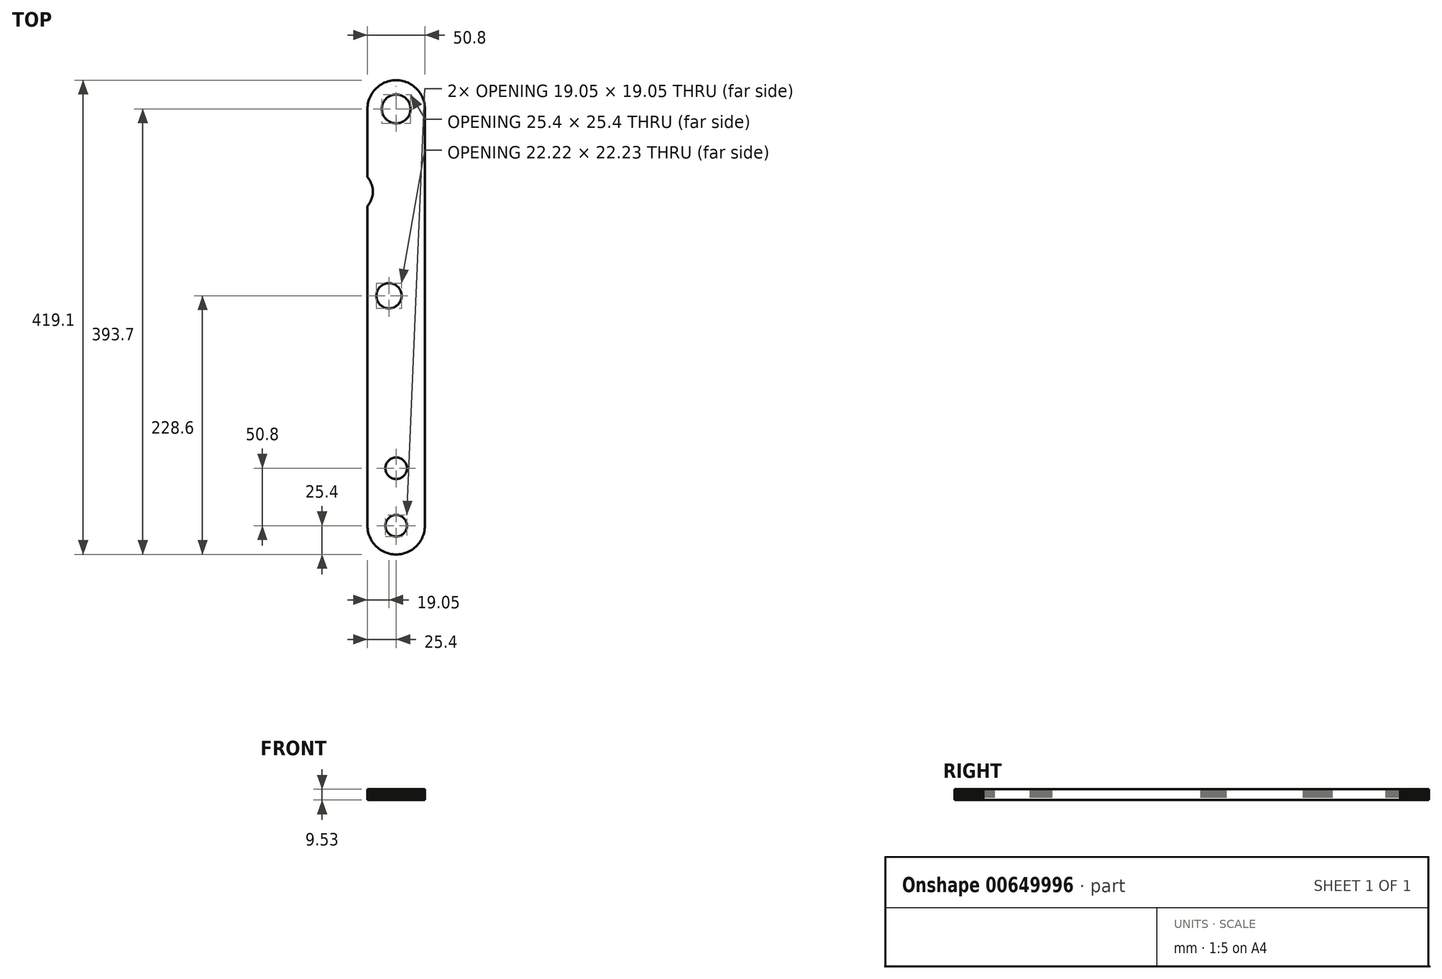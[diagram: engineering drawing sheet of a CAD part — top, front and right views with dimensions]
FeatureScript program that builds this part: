
annotation { "Feature Type Name" : "Feature", "Feature Type Description" : "" }
export const myFeature = defineFeature(function(context is Context, id is Id, definition is map)
    precondition{}
    {
        {
            var Q0;
            Q0=qCreatedBy(makeId("Top.planeOp"),FACE);
            var sketch = newSketch(context, id + "F0", { "sketchPlane" : qUnion([Q0])});
            skLineSegment(sketch, "E0", {"start": v(25.4, 184.15) * mm, "end": v(25.36, 185.63) * mm});
            skLineSegment(sketch, "E1", {"start": v(25.36, 185.63) * mm, "end": v(25.23, 187.1) * mm});
            skLineSegment(sketch, "E2", {"start": v(25.23, 187.1) * mm, "end": v(25.02, 188.55) * mm});
            skLineSegment(sketch, "E3", {"start": v(25.02, 188.55) * mm, "end": v(24.72, 190.01) * mm});
            skLineSegment(sketch, "E4", {"start": v(24.72, 190.01) * mm, "end": v(24.34, 191.43) * mm});
            skLineSegment(sketch, "E5", {"start": v(24.34, 191.43) * mm, "end": v(23.88, 192.83) * mm});
            skLineSegment(sketch, "E6", {"start": v(23.88, 192.83) * mm, "end": v(23.33, 194.2) * mm});
            skLineSegment(sketch, "E7", {"start": v(23.33, 194.2) * mm, "end": v(22.71, 195.56) * mm});
            skLineSegment(sketch, "E8", {"start": v(22.71, 195.56) * mm, "end": v(22.01, 196.85) * mm});
            skLineSegment(sketch, "E9", {"start": v(22.01, 196.85) * mm, "end": v(21.23, 198.1) * mm});
            skLineSegment(sketch, "E10", {"start": v(21.23, 198.1) * mm, "end": v(20.38, 199.33) * mm});
            skLineSegment(sketch, "E11", {"start": v(20.38, 199.33) * mm, "end": v(19.47, 200.47) * mm});
            skLineSegment(sketch, "E12", {"start": v(19.47, 200.47) * mm, "end": v(18.48, 201.57) * mm});
            skLineSegment(sketch, "E13", {"start": v(18.48, 201.57) * mm, "end": v(17.44, 202.63) * mm});
            skLineSegment(sketch, "E14", {"start": v(17.44, 202.63) * mm, "end": v(16.34, 203.6) * mm});
            skLineSegment(sketch, "E15", {"start": v(16.34, 203.6) * mm, "end": v(15.18, 204.53) * mm});
            skLineSegment(sketch, "E16", {"start": v(15.18, 204.53) * mm, "end": v(13.97, 205.38) * mm});
            skLineSegment(sketch, "E17", {"start": v(13.97, 205.38) * mm, "end": v(12.7, 206.14) * mm});
            skLineSegment(sketch, "E18", {"start": v(12.7, 206.14) * mm, "end": v(11.4, 206.84) * mm});
            skLineSegment(sketch, "E19", {"start": v(11.4, 206.84) * mm, "end": v(10.08, 207.48) * mm});
            skLineSegment(sketch, "E20", {"start": v(10.08, 207.48) * mm, "end": v(8.7, 208.03) * mm});
            skLineSegment(sketch, "E21", {"start": v(8.7, 208.03) * mm, "end": v(7.3, 208.5) * mm});
            skLineSegment(sketch, "E22", {"start": v(7.3, 208.5) * mm, "end": v(5.86, 208.87) * mm});
            skLineSegment(sketch, "E23", {"start": v(5.86, 208.87) * mm, "end": v(4.42, 209.17) * mm});
            skLineSegment(sketch, "E24", {"start": v(4.42, 209.17) * mm, "end": v(2.96, 209.38) * mm});
            skLineSegment(sketch, "E25", {"start": v(2.96, 209.38) * mm, "end": v(1.48, 209.5) * mm});
            skLineSegment(sketch, "E26", {"start": v(1.48, 209.5) * mm, "end": v(0, 209.55) * mm});
            skLineSegment(sketch, "E27", {"start": v(0, 209.55) * mm, "end": v(-1.46, 209.5) * mm});
            skLineSegment(sketch, "E28", {"start": v(-1.46, 209.5) * mm, "end": v(-2.94, 209.38) * mm});
            skLineSegment(sketch, "E29", {"start": v(-2.94, 209.38) * mm, "end": v(-4.4, 209.17) * mm});
            skLineSegment(sketch, "E30", {"start": v(-4.4, 209.17) * mm, "end": v(-5.84, 208.87) * mm});
            skLineSegment(sketch, "E31", {"start": v(-5.84, 208.87) * mm, "end": v(-7.28, 208.5) * mm});
            skLineSegment(sketch, "E32", {"start": v(-7.28, 208.5) * mm, "end": v(-8.68, 208.03) * mm});
            skLineSegment(sketch, "E33", {"start": v(-8.68, 208.03) * mm, "end": v(-10.05, 207.48) * mm});
            skLineSegment(sketch, "E34", {"start": v(-10.05, 207.48) * mm, "end": v(-11.39, 206.84) * mm});
            skLineSegment(sketch, "E35", {"start": v(-11.39, 206.84) * mm, "end": v(-12.7, 206.14) * mm});
            skLineSegment(sketch, "E36", {"start": v(-12.7, 206.14) * mm, "end": v(-13.95, 205.38) * mm});
            skLineSegment(sketch, "E37", {"start": v(-13.95, 205.38) * mm, "end": v(-15.16, 204.53) * mm});
            skLineSegment(sketch, "E38", {"start": v(-15.16, 204.53) * mm, "end": v(-16.32, 203.6) * mm});
            skLineSegment(sketch, "E39", {"start": v(-16.32, 203.6) * mm, "end": v(-17.42, 202.63) * mm});
            skLineSegment(sketch, "E40", {"start": v(-17.42, 202.63) * mm, "end": v(-18.46, 201.57) * mm});
            skLineSegment(sketch, "E41", {"start": v(-18.46, 201.57) * mm, "end": v(-19.45, 200.47) * mm});
            skLineSegment(sketch, "E42", {"start": v(-19.45, 200.47) * mm, "end": v(-20.36, 199.33) * mm});
            skLineSegment(sketch, "E43", {"start": v(-20.36, 199.33) * mm, "end": v(-21.2, 198.1) * mm});
            skLineSegment(sketch, "E44", {"start": v(-21.2, 198.1) * mm, "end": v(-22, 196.85) * mm});
            skLineSegment(sketch, "E45", {"start": v(-22, 196.85) * mm, "end": v(-22.7, 195.56) * mm});
            skLineSegment(sketch, "E46", {"start": v(-22.7, 195.56) * mm, "end": v(-23.3, 194.2) * mm});
            skLineSegment(sketch, "E47", {"start": v(-23.3, 194.2) * mm, "end": v(-23.85, 192.83) * mm});
            skLineSegment(sketch, "E48", {"start": v(-23.85, 192.83) * mm, "end": v(-24.32, 191.43) * mm});
            skLineSegment(sketch, "E49", {"start": v(-24.32, 191.43) * mm, "end": v(-24.7, 190.01) * mm});
            skLineSegment(sketch, "E50", {"start": v(-24.7, 190.01) * mm, "end": v(-25, 188.55) * mm});
            skLineSegment(sketch, "E51", {"start": v(-25, 188.55) * mm, "end": v(-25.2, 187.1) * mm});
            skLineSegment(sketch, "E52", {"start": v(-25.2, 187.1) * mm, "end": v(-25.34, 185.63) * mm});
            skLineSegment(sketch, "E53", {"start": v(-25.34, 185.63) * mm, "end": v(-25.4, 184.15) * mm});
            skLineSegment(sketch, "E54", {"start": v(0, -209.55) * mm, "end": v(1.48, -209.5) * mm});
            skLineSegment(sketch, "E55", {"start": v(1.48, -209.5) * mm, "end": v(2.96, -209.38) * mm});
            skLineSegment(sketch, "E56", {"start": v(2.96, -209.38) * mm, "end": v(4.42, -209.17) * mm});
            skLineSegment(sketch, "E57", {"start": v(4.42, -209.17) * mm, "end": v(5.86, -208.87) * mm});
            skLineSegment(sketch, "E58", {"start": v(5.86, -208.87) * mm, "end": v(7.3, -208.5) * mm});
            skLineSegment(sketch, "E59", {"start": v(7.3, -208.5) * mm, "end": v(8.7, -208.03) * mm});
            skLineSegment(sketch, "E60", {"start": v(8.7, -208.03) * mm, "end": v(10.08, -207.48) * mm});
            skLineSegment(sketch, "E61", {"start": v(10.08, -207.48) * mm, "end": v(11.4, -206.84) * mm});
            skLineSegment(sketch, "E62", {"start": v(11.4, -206.84) * mm, "end": v(12.7, -206.14) * mm});
            skLineSegment(sketch, "E63", {"start": v(12.7, -206.14) * mm, "end": v(13.97, -205.38) * mm});
            skLineSegment(sketch, "E64", {"start": v(13.97, -205.38) * mm, "end": v(15.18, -204.53) * mm});
            skLineSegment(sketch, "E65", {"start": v(15.18, -204.53) * mm, "end": v(16.34, -203.6) * mm});
            skLineSegment(sketch, "E66", {"start": v(16.34, -203.6) * mm, "end": v(17.44, -202.63) * mm});
            skLineSegment(sketch, "E67", {"start": v(17.44, -202.63) * mm, "end": v(18.48, -201.57) * mm});
            skLineSegment(sketch, "E68", {"start": v(18.48, -201.57) * mm, "end": v(19.47, -200.47) * mm});
            skLineSegment(sketch, "E69", {"start": v(19.47, -200.47) * mm, "end": v(20.38, -199.33) * mm});
            skLineSegment(sketch, "E70", {"start": v(20.38, -199.33) * mm, "end": v(21.23, -198.1) * mm});
            skLineSegment(sketch, "E71", {"start": v(21.23, -198.1) * mm, "end": v(22.01, -196.85) * mm});
            skLineSegment(sketch, "E72", {"start": v(22.01, -196.85) * mm, "end": v(22.71, -195.56) * mm});
            skLineSegment(sketch, "E73", {"start": v(22.71, -195.56) * mm, "end": v(23.33, -194.2) * mm});
            skLineSegment(sketch, "E74", {"start": v(23.33, -194.2) * mm, "end": v(23.88, -192.83) * mm});
            skLineSegment(sketch, "E75", {"start": v(23.88, -192.83) * mm, "end": v(24.34, -191.43) * mm});
            skLineSegment(sketch, "E76", {"start": v(24.34, -191.43) * mm, "end": v(24.72, -190.01) * mm});
            skLineSegment(sketch, "E77", {"start": v(24.72, -190.01) * mm, "end": v(25.02, -188.55) * mm});
            skLineSegment(sketch, "E78", {"start": v(25.02, -188.55) * mm, "end": v(25.23, -187.1) * mm});
            skLineSegment(sketch, "E79", {"start": v(25.23, -187.1) * mm, "end": v(25.36, -185.63) * mm});
            skLineSegment(sketch, "E80", {"start": v(25.36, -185.63) * mm, "end": v(25.4, -184.15) * mm});
            skLineSegment(sketch, "E81", {"start": v(-25.4, -184.15) * mm, "end": v(-25.34, -185.63) * mm});
            skLineSegment(sketch, "E82", {"start": v(-25.34, -185.63) * mm, "end": v(-25.2, -187.1) * mm});
            skLineSegment(sketch, "E83", {"start": v(-25.2, -187.1) * mm, "end": v(-25, -188.55) * mm});
            skLineSegment(sketch, "E84", {"start": v(-25, -188.55) * mm, "end": v(-24.7, -190.01) * mm});
            skLineSegment(sketch, "E85", {"start": v(-24.7, -190.01) * mm, "end": v(-24.32, -191.43) * mm});
            skLineSegment(sketch, "E86", {"start": v(-24.32, -191.43) * mm, "end": v(-23.85, -192.83) * mm});
            skLineSegment(sketch, "E87", {"start": v(-23.85, -192.83) * mm, "end": v(-23.3, -194.2) * mm});
            skLineSegment(sketch, "E88", {"start": v(-23.3, -194.2) * mm, "end": v(-22.7, -195.56) * mm});
            skLineSegment(sketch, "E89", {"start": v(-22.7, -195.56) * mm, "end": v(-22, -196.85) * mm});
            skLineSegment(sketch, "E90", {"start": v(-22, -196.85) * mm, "end": v(-21.2, -198.1) * mm});
            skLineSegment(sketch, "E91", {"start": v(-21.2, -198.1) * mm, "end": v(-20.36, -199.33) * mm});
            skLineSegment(sketch, "E92", {"start": v(-20.36, -199.33) * mm, "end": v(-19.45, -200.47) * mm});
            skLineSegment(sketch, "E93", {"start": v(-19.45, -200.47) * mm, "end": v(-18.46, -201.57) * mm});
            skLineSegment(sketch, "E94", {"start": v(-18.46, -201.57) * mm, "end": v(-17.42, -202.63) * mm});
            skLineSegment(sketch, "E95", {"start": v(-17.42, -202.63) * mm, "end": v(-16.32, -203.6) * mm});
            skLineSegment(sketch, "E96", {"start": v(-16.32, -203.6) * mm, "end": v(-15.16, -204.53) * mm});
            skLineSegment(sketch, "E97", {"start": v(-15.16, -204.53) * mm, "end": v(-13.95, -205.38) * mm});
            skLineSegment(sketch, "E98", {"start": v(-13.95, -205.38) * mm, "end": v(-12.7, -206.14) * mm});
            skLineSegment(sketch, "E99", {"start": v(-12.7, -206.14) * mm, "end": v(-11.39, -206.84) * mm});
            skLineSegment(sketch, "E100", {"start": v(-11.39, -206.84) * mm, "end": v(-10.05, -207.48) * mm});
            skLineSegment(sketch, "E101", {"start": v(-10.05, -207.48) * mm, "end": v(-8.68, -208.03) * mm});
            skLineSegment(sketch, "E102", {"start": v(-8.68, -208.03) * mm, "end": v(-7.28, -208.5) * mm});
            skLineSegment(sketch, "E103", {"start": v(-7.28, -208.5) * mm, "end": v(-5.84, -208.87) * mm});
            skLineSegment(sketch, "E104", {"start": v(-5.84, -208.87) * mm, "end": v(-4.4, -209.17) * mm});
            skLineSegment(sketch, "E105", {"start": v(-4.4, -209.17) * mm, "end": v(-2.94, -209.38) * mm});
            skLineSegment(sketch, "E106", {"start": v(-2.94, -209.38) * mm, "end": v(-1.46, -209.5) * mm});
            skLineSegment(sketch, "E107", {"start": v(-1.46, -209.5) * mm, "end": v(0, -209.55) * mm});
            skLineSegment(sketch, "E108", {"start": v(0, -142.88) * mm, "end": v(0.89, -142.83) * mm});
            skLineSegment(sketch, "E109", {"start": v(0.89, -142.83) * mm, "end": v(1.76, -142.7) * mm});
            skLineSegment(sketch, "E110", {"start": v(1.76, -142.7) * mm, "end": v(2.62, -142.52) * mm});
            skLineSegment(sketch, "E111", {"start": v(2.62, -142.52) * mm, "end": v(3.45, -142.24) * mm});
            skLineSegment(sketch, "E112", {"start": v(3.45, -142.24) * mm, "end": v(4.25, -141.88) * mm});
            skLineSegment(sketch, "E113", {"start": v(4.25, -141.88) * mm, "end": v(5.02, -141.46) * mm});
            skLineSegment(sketch, "E114", {"start": v(5.02, -141.46) * mm, "end": v(5.76, -140.95) * mm});
            skLineSegment(sketch, "E115", {"start": v(5.76, -140.95) * mm, "end": v(6.43, -140.4) * mm});
            skLineSegment(sketch, "E116", {"start": v(6.43, -140.4) * mm, "end": v(7.05, -139.76) * mm});
            skLineSegment(sketch, "E117", {"start": v(7.05, -139.76) * mm, "end": v(7.62, -139.09) * mm});
            skLineSegment(sketch, "E118", {"start": v(7.62, -139.09) * mm, "end": v(8.1, -138.37) * mm});
            skLineSegment(sketch, "E119", {"start": v(8.1, -138.37) * mm, "end": v(8.53, -137.6) * mm});
            skLineSegment(sketch, "E120", {"start": v(8.53, -137.6) * mm, "end": v(8.89, -136.8) * mm});
            skLineSegment(sketch, "E121", {"start": v(8.89, -136.8) * mm, "end": v(9.17, -135.95) * mm});
            skLineSegment(sketch, "E122", {"start": v(9.17, -135.95) * mm, "end": v(9.38, -135.1) * mm});
            skLineSegment(sketch, "E123", {"start": v(9.38, -135.1) * mm, "end": v(9.5, -134.24) * mm});
            skLineSegment(sketch, "E124", {"start": v(9.5, -134.24) * mm, "end": v(9.53, -133.35) * mm});
            skLineSegment(sketch, "E125", {"start": v(9.53, -133.35) * mm, "end": v(9.5, -132.46) * mm});
            skLineSegment(sketch, "E126", {"start": v(9.5, -132.46) * mm, "end": v(9.38, -131.6) * mm});
            skLineSegment(sketch, "E127", {"start": v(9.38, -131.6) * mm, "end": v(9.17, -130.75) * mm});
            skLineSegment(sketch, "E128", {"start": v(9.17, -130.75) * mm, "end": v(8.89, -129.9) * mm});
            skLineSegment(sketch, "E129", {"start": v(8.89, -129.9) * mm, "end": v(8.53, -129.1) * mm});
            skLineSegment(sketch, "E130", {"start": v(8.53, -129.1) * mm, "end": v(8.1, -128.33) * mm});
            skLineSegment(sketch, "E131", {"start": v(8.1, -128.33) * mm, "end": v(7.62, -127.61) * mm});
            skLineSegment(sketch, "E132", {"start": v(7.62, -127.61) * mm, "end": v(7.05, -126.94) * mm});
            skLineSegment(sketch, "E133", {"start": v(7.05, -126.94) * mm, "end": v(6.43, -126.3) * mm});
            skLineSegment(sketch, "E134", {"start": v(6.43, -126.3) * mm, "end": v(5.76, -125.75) * mm});
            skLineSegment(sketch, "E135", {"start": v(5.76, -125.75) * mm, "end": v(5.02, -125.24) * mm});
            skLineSegment(sketch, "E136", {"start": v(5.02, -125.24) * mm, "end": v(4.25, -124.82) * mm});
            skLineSegment(sketch, "E137", {"start": v(4.25, -124.82) * mm, "end": v(3.45, -124.46) * mm});
            skLineSegment(sketch, "E138", {"start": v(3.45, -124.46) * mm, "end": v(2.62, -124.18) * mm});
            skLineSegment(sketch, "E139", {"start": v(2.62, -124.18) * mm, "end": v(1.76, -124) * mm});
            skLineSegment(sketch, "E140", {"start": v(1.76, -124) * mm, "end": v(0.89, -123.87) * mm});
            skLineSegment(sketch, "E141", {"start": v(0.89, -123.87) * mm, "end": v(0, -123.83) * mm});
            skLineSegment(sketch, "E142", {"start": v(0, -123.83) * mm, "end": v(-0.87, -123.87) * mm});
            skLineSegment(sketch, "E143", {"start": v(-0.87, -123.87) * mm, "end": v(-1.74, -124) * mm});
            skLineSegment(sketch, "E144", {"start": v(-1.74, -124) * mm, "end": v(-2.6, -124.18) * mm});
            skLineSegment(sketch, "E145", {"start": v(-2.6, -124.18) * mm, "end": v(-3.43, -124.46) * mm});
            skLineSegment(sketch, "E146", {"start": v(-3.43, -124.46) * mm, "end": v(-4.23, -124.82) * mm});
            skLineSegment(sketch, "E147", {"start": v(-4.23, -124.82) * mm, "end": v(-5, -125.24) * mm});
            skLineSegment(sketch, "E148", {"start": v(-5, -125.24) * mm, "end": v(-5.74, -125.75) * mm});
            skLineSegment(sketch, "E149", {"start": v(-5.74, -125.75) * mm, "end": v(-6.41, -126.3) * mm});
            skLineSegment(sketch, "E150", {"start": v(-6.41, -126.3) * mm, "end": v(-7.03, -126.94) * mm});
            skLineSegment(sketch, "E151", {"start": v(-7.03, -126.94) * mm, "end": v(-7.6, -127.61) * mm});
            skLineSegment(sketch, "E152", {"start": v(-7.6, -127.61) * mm, "end": v(-8.09, -128.33) * mm});
            skLineSegment(sketch, "E153", {"start": v(-8.09, -128.33) * mm, "end": v(-8.5, -129.1) * mm});
            skLineSegment(sketch, "E154", {"start": v(-8.5, -129.1) * mm, "end": v(-8.87, -129.9) * mm});
            skLineSegment(sketch, "E155", {"start": v(-8.87, -129.9) * mm, "end": v(-9.14, -130.75) * mm});
            skLineSegment(sketch, "E156", {"start": v(-9.14, -130.75) * mm, "end": v(-9.36, -131.6) * mm});
            skLineSegment(sketch, "E157", {"start": v(-9.36, -131.6) * mm, "end": v(-9.48, -132.46) * mm});
            skLineSegment(sketch, "E158", {"start": v(-9.48, -132.46) * mm, "end": v(-9.53, -133.35) * mm});
            skLineSegment(sketch, "E159", {"start": v(-9.53, -133.35) * mm, "end": v(-9.48, -134.24) * mm});
            skLineSegment(sketch, "E160", {"start": v(-9.48, -134.24) * mm, "end": v(-9.36, -135.1) * mm});
            skLineSegment(sketch, "E161", {"start": v(-9.36, -135.1) * mm, "end": v(-9.14, -135.95) * mm});
            skLineSegment(sketch, "E162", {"start": v(-9.14, -135.95) * mm, "end": v(-8.87, -136.8) * mm});
            skLineSegment(sketch, "E163", {"start": v(-8.87, -136.8) * mm, "end": v(-8.5, -137.6) * mm});
            skLineSegment(sketch, "E164", {"start": v(-8.5, -137.6) * mm, "end": v(-8.09, -138.37) * mm});
            skLineSegment(sketch, "E165", {"start": v(-8.09, -138.37) * mm, "end": v(-7.6, -139.09) * mm});
            skLineSegment(sketch, "E166", {"start": v(-7.6, -139.09) * mm, "end": v(-7.03, -139.76) * mm});
            skLineSegment(sketch, "E167", {"start": v(-7.03, -139.76) * mm, "end": v(-6.41, -140.4) * mm});
            skLineSegment(sketch, "E168", {"start": v(-6.41, -140.4) * mm, "end": v(-5.74, -140.95) * mm});
            skLineSegment(sketch, "E169", {"start": v(-5.74, -140.95) * mm, "end": v(-5, -141.46) * mm});
            skLineSegment(sketch, "E170", {"start": v(-5, -141.46) * mm, "end": v(-4.23, -141.88) * mm});
            skLineSegment(sketch, "E171", {"start": v(-4.23, -141.88) * mm, "end": v(-3.43, -142.24) * mm});
            skLineSegment(sketch, "E172", {"start": v(-3.43, -142.24) * mm, "end": v(-2.6, -142.52) * mm});
            skLineSegment(sketch, "E173", {"start": v(-2.6, -142.52) * mm, "end": v(-1.74, -142.7) * mm});
            skLineSegment(sketch, "E174", {"start": v(-1.74, -142.7) * mm, "end": v(-0.87, -142.83) * mm});
            skLineSegment(sketch, "E175", {"start": v(-0.87, -142.83) * mm, "end": v(0, -142.88) * mm});
            skLineSegment(sketch, "E176", {"start": v(0, -193.68) * mm, "end": v(0.89, -193.63) * mm});
            skLineSegment(sketch, "E177", {"start": v(0.89, -193.63) * mm, "end": v(1.76, -193.5) * mm});
            skLineSegment(sketch, "E178", {"start": v(1.76, -193.5) * mm, "end": v(2.62, -193.32) * mm});
            skLineSegment(sketch, "E179", {"start": v(2.62, -193.32) * mm, "end": v(3.45, -193.04) * mm});
            skLineSegment(sketch, "E180", {"start": v(3.45, -193.04) * mm, "end": v(4.25, -192.68) * mm});
            skLineSegment(sketch, "E181", {"start": v(4.25, -192.68) * mm, "end": v(5.02, -192.26) * mm});
            skLineSegment(sketch, "E182", {"start": v(5.02, -192.26) * mm, "end": v(5.76, -191.75) * mm});
            skLineSegment(sketch, "E183", {"start": v(5.76, -191.75) * mm, "end": v(6.43, -191.2) * mm});
            skLineSegment(sketch, "E184", {"start": v(6.43, -191.2) * mm, "end": v(7.05, -190.56) * mm});
            skLineSegment(sketch, "E185", {"start": v(7.05, -190.56) * mm, "end": v(7.62, -189.89) * mm});
            skLineSegment(sketch, "E186", {"start": v(7.62, -189.89) * mm, "end": v(8.1, -189.17) * mm});
            skLineSegment(sketch, "E187", {"start": v(8.1, -189.17) * mm, "end": v(8.53, -188.4) * mm});
            skLineSegment(sketch, "E188", {"start": v(8.53, -188.4) * mm, "end": v(8.89, -187.6) * mm});
            skLineSegment(sketch, "E189", {"start": v(8.89, -187.6) * mm, "end": v(9.17, -186.75) * mm});
            skLineSegment(sketch, "E190", {"start": v(9.17, -186.75) * mm, "end": v(9.38, -185.9) * mm});
            skLineSegment(sketch, "E191", {"start": v(9.38, -185.9) * mm, "end": v(9.5, -185.04) * mm});
            skLineSegment(sketch, "E192", {"start": v(9.5, -185.04) * mm, "end": v(9.53, -184.15) * mm});
            skLineSegment(sketch, "E193", {"start": v(9.53, -184.15) * mm, "end": v(9.5, -183.26) * mm});
            skLineSegment(sketch, "E194", {"start": v(9.5, -183.26) * mm, "end": v(9.38, -182.4) * mm});
            skLineSegment(sketch, "E195", {"start": v(9.38, -182.4) * mm, "end": v(9.17, -181.55) * mm});
            skLineSegment(sketch, "E196", {"start": v(9.17, -181.55) * mm, "end": v(8.89, -180.7) * mm});
            skLineSegment(sketch, "E197", {"start": v(8.89, -180.7) * mm, "end": v(8.53, -179.9) * mm});
            skLineSegment(sketch, "E198", {"start": v(8.53, -179.9) * mm, "end": v(8.1, -179.13) * mm});
            skLineSegment(sketch, "E199", {"start": v(8.1, -179.13) * mm, "end": v(7.62, -178.41) * mm});
            skLineSegment(sketch, "E200", {"start": v(7.62, -178.41) * mm, "end": v(7.05, -177.74) * mm});
            skLineSegment(sketch, "E201", {"start": v(7.05, -177.74) * mm, "end": v(6.43, -177.1) * mm});
            skLineSegment(sketch, "E202", {"start": v(6.43, -177.1) * mm, "end": v(5.76, -176.55) * mm});
            skLineSegment(sketch, "E203", {"start": v(5.76, -176.55) * mm, "end": v(5.02, -176.04) * mm});
            skLineSegment(sketch, "E204", {"start": v(5.02, -176.04) * mm, "end": v(4.25, -175.62) * mm});
            skLineSegment(sketch, "E205", {"start": v(4.25, -175.62) * mm, "end": v(3.45, -175.26) * mm});
            skLineSegment(sketch, "E206", {"start": v(3.45, -175.26) * mm, "end": v(2.62, -174.98) * mm});
            skLineSegment(sketch, "E207", {"start": v(2.62, -174.98) * mm, "end": v(1.76, -174.8) * mm});
            skLineSegment(sketch, "E208", {"start": v(1.76, -174.8) * mm, "end": v(0.89, -174.67) * mm});
            skLineSegment(sketch, "E209", {"start": v(0.89, -174.67) * mm, "end": v(0, -174.63) * mm});
            skLineSegment(sketch, "E210", {"start": v(0, -174.63) * mm, "end": v(-0.87, -174.67) * mm});
            skLineSegment(sketch, "E211", {"start": v(-0.87, -174.67) * mm, "end": v(-1.74, -174.8) * mm});
            skLineSegment(sketch, "E212", {"start": v(-1.74, -174.8) * mm, "end": v(-2.6, -174.98) * mm});
            skLineSegment(sketch, "E213", {"start": v(-2.6, -174.98) * mm, "end": v(-3.43, -175.26) * mm});
            skLineSegment(sketch, "E214", {"start": v(-3.43, -175.26) * mm, "end": v(-4.23, -175.62) * mm});
            skLineSegment(sketch, "E215", {"start": v(-4.23, -175.62) * mm, "end": v(-5, -176.04) * mm});
            skLineSegment(sketch, "E216", {"start": v(-5, -176.04) * mm, "end": v(-5.74, -176.55) * mm});
            skLineSegment(sketch, "E217", {"start": v(-5.74, -176.55) * mm, "end": v(-6.41, -177.1) * mm});
            skLineSegment(sketch, "E218", {"start": v(-6.41, -177.1) * mm, "end": v(-7.03, -177.74) * mm});
            skLineSegment(sketch, "E219", {"start": v(-7.03, -177.74) * mm, "end": v(-7.6, -178.41) * mm});
            skLineSegment(sketch, "E220", {"start": v(-7.6, -178.41) * mm, "end": v(-8.09, -179.13) * mm});
            skLineSegment(sketch, "E221", {"start": v(-8.09, -179.13) * mm, "end": v(-8.5, -179.9) * mm});
            skLineSegment(sketch, "E222", {"start": v(-8.5, -179.9) * mm, "end": v(-8.87, -180.7) * mm});
            skLineSegment(sketch, "E223", {"start": v(-8.87, -180.7) * mm, "end": v(-9.14, -181.55) * mm});
            skLineSegment(sketch, "E224", {"start": v(-9.14, -181.55) * mm, "end": v(-9.36, -182.4) * mm});
            skLineSegment(sketch, "E225", {"start": v(-9.36, -182.4) * mm, "end": v(-9.48, -183.26) * mm});
            skLineSegment(sketch, "E226", {"start": v(-9.48, -183.26) * mm, "end": v(-9.53, -184.15) * mm});
            skLineSegment(sketch, "E227", {"start": v(-9.53, -184.15) * mm, "end": v(-9.48, -185.04) * mm});
            skLineSegment(sketch, "E228", {"start": v(-9.48, -185.04) * mm, "end": v(-9.36, -185.9) * mm});
            skLineSegment(sketch, "E229", {"start": v(-9.36, -185.9) * mm, "end": v(-9.14, -186.75) * mm});
            skLineSegment(sketch, "E230", {"start": v(-9.14, -186.75) * mm, "end": v(-8.87, -187.6) * mm});
            skLineSegment(sketch, "E231", {"start": v(-8.87, -187.6) * mm, "end": v(-8.5, -188.4) * mm});
            skLineSegment(sketch, "E232", {"start": v(-8.5, -188.4) * mm, "end": v(-8.09, -189.17) * mm});
            skLineSegment(sketch, "E233", {"start": v(-8.09, -189.17) * mm, "end": v(-7.6, -189.89) * mm});
            skLineSegment(sketch, "E234", {"start": v(-7.6, -189.89) * mm, "end": v(-7.03, -190.56) * mm});
            skLineSegment(sketch, "E235", {"start": v(-7.03, -190.56) * mm, "end": v(-6.41, -191.2) * mm});
            skLineSegment(sketch, "E236", {"start": v(-6.41, -191.2) * mm, "end": v(-5.74, -191.75) * mm});
            skLineSegment(sketch, "E237", {"start": v(-5.74, -191.75) * mm, "end": v(-5, -192.26) * mm});
            skLineSegment(sketch, "E238", {"start": v(-5, -192.26) * mm, "end": v(-4.23, -192.68) * mm});
            skLineSegment(sketch, "E239", {"start": v(-4.23, -192.68) * mm, "end": v(-3.43, -193.04) * mm});
            skLineSegment(sketch, "E240", {"start": v(-3.43, -193.04) * mm, "end": v(-2.6, -193.32) * mm});
            skLineSegment(sketch, "E241", {"start": v(-2.6, -193.32) * mm, "end": v(-1.74, -193.5) * mm});
            skLineSegment(sketch, "E242", {"start": v(-1.74, -193.5) * mm, "end": v(-0.87, -193.63) * mm});
            skLineSegment(sketch, "E243", {"start": v(-0.87, -193.63) * mm, "end": v(0, -193.68) * mm});
            skLineSegment(sketch, "E244", {"start": v(25.4, 184.15) * mm, "end": v(25.4, -184.15) * mm});
            skLineSegment(sketch, "E245", {"start": v(-25.4, 98.42) * mm, "end": v(-25.4, -184.15) * mm});
            skLineSegment(sketch, "E246", {"start": v(-25.4, 184.15) * mm, "end": v(-25.4, 123.82) * mm});
            skLineSegment(sketch, "E247", {"start": v(0, 171.45) * mm, "end": v(1.06, 171.5) * mm});
            skLineSegment(sketch, "E248", {"start": v(1.06, 171.5) * mm, "end": v(2.1, 171.62) * mm});
            skLineSegment(sketch, "E249", {"start": v(2.1, 171.62) * mm, "end": v(3.13, 171.83) * mm});
            skLineSegment(sketch, "E250", {"start": v(3.13, 171.83) * mm, "end": v(4.13, 172.15) * mm});
            skLineSegment(sketch, "E251", {"start": v(4.13, 172.15) * mm, "end": v(5.1, 172.53) * mm});
            skLineSegment(sketch, "E252", {"start": v(5.1, 172.53) * mm, "end": v(6.05, 172.97) * mm});
            skLineSegment(sketch, "E253", {"start": v(6.05, 172.97) * mm, "end": v(6.96, 173.52) * mm});
            skLineSegment(sketch, "E254", {"start": v(6.96, 173.52) * mm, "end": v(7.81, 174.14) * mm});
            skLineSegment(sketch, "E255", {"start": v(7.81, 174.14) * mm, "end": v(8.61, 174.82) * mm});
            skLineSegment(sketch, "E256", {"start": v(8.61, 174.82) * mm, "end": v(9.36, 175.56) * mm});
            skLineSegment(sketch, "E257", {"start": v(9.36, 175.56) * mm, "end": v(10.03, 176.34) * mm});
            skLineSegment(sketch, "E258", {"start": v(10.03, 176.34) * mm, "end": v(10.65, 177.2) * mm});
            skLineSegment(sketch, "E259", {"start": v(10.65, 177.2) * mm, "end": v(11.18, 178.1) * mm});
            skLineSegment(sketch, "E260", {"start": v(11.18, 178.1) * mm, "end": v(11.64, 179.05) * mm});
            skLineSegment(sketch, "E261", {"start": v(11.64, 179.05) * mm, "end": v(12.02, 180.02) * mm});
            skLineSegment(sketch, "E262", {"start": v(12.02, 180.02) * mm, "end": v(12.32, 181.04) * mm});
            skLineSegment(sketch, "E263", {"start": v(12.32, 181.04) * mm, "end": v(12.53, 182.05) * mm});
            skLineSegment(sketch, "E264", {"start": v(12.53, 182.05) * mm, "end": v(12.66, 183.1) * mm});
            skLineSegment(sketch, "E265", {"start": v(12.66, 183.1) * mm, "end": v(12.7, 184.15) * mm});
            skLineSegment(sketch, "E266", {"start": v(12.7, 184.15) * mm, "end": v(12.66, 185.2) * mm});
            skLineSegment(sketch, "E267", {"start": v(12.66, 185.2) * mm, "end": v(12.53, 186.25) * mm});
            skLineSegment(sketch, "E268", {"start": v(12.53, 186.25) * mm, "end": v(12.32, 187.26) * mm});
            skLineSegment(sketch, "E269", {"start": v(12.32, 187.26) * mm, "end": v(12.02, 188.28) * mm});
            skLineSegment(sketch, "E270", {"start": v(12.02, 188.28) * mm, "end": v(11.64, 189.25) * mm});
            skLineSegment(sketch, "E271", {"start": v(11.64, 189.25) * mm, "end": v(11.18, 190.2) * mm});
            skLineSegment(sketch, "E272", {"start": v(11.18, 190.2) * mm, "end": v(10.65, 191.1) * mm});
            skLineSegment(sketch, "E273", {"start": v(10.65, 191.1) * mm, "end": v(10.03, 191.96) * mm});
            skLineSegment(sketch, "E274", {"start": v(10.03, 191.96) * mm, "end": v(9.36, 192.74) * mm});
            skLineSegment(sketch, "E275", {"start": v(9.36, 192.74) * mm, "end": v(8.61, 193.48) * mm});
            skLineSegment(sketch, "E276", {"start": v(8.61, 193.48) * mm, "end": v(7.81, 194.16) * mm});
            skLineSegment(sketch, "E277", {"start": v(7.81, 194.16) * mm, "end": v(6.96, 194.78) * mm});
            skLineSegment(sketch, "E278", {"start": v(6.96, 194.78) * mm, "end": v(6.05, 195.33) * mm});
            skLineSegment(sketch, "E279", {"start": v(6.05, 195.33) * mm, "end": v(5.1, 195.77) * mm});
            skLineSegment(sketch, "E280", {"start": v(5.1, 195.77) * mm, "end": v(4.13, 196.15) * mm});
            skLineSegment(sketch, "E281", {"start": v(4.13, 196.15) * mm, "end": v(3.13, 196.47) * mm});
            skLineSegment(sketch, "E282", {"start": v(3.13, 196.47) * mm, "end": v(2.1, 196.68) * mm});
            skLineSegment(sketch, "E283", {"start": v(2.1, 196.68) * mm, "end": v(1.06, 196.8) * mm});
            skLineSegment(sketch, "E284", {"start": v(1.06, 196.8) * mm, "end": v(0, 196.85) * mm});
            skLineSegment(sketch, "E285", {"start": v(0, 196.85) * mm, "end": v(-1.04, 196.8) * mm});
            skLineSegment(sketch, "E286", {"start": v(-1.04, 196.8) * mm, "end": v(-2.07, 196.68) * mm});
            skLineSegment(sketch, "E287", {"start": v(-2.07, 196.68) * mm, "end": v(-3.11, 196.47) * mm});
            skLineSegment(sketch, "E288", {"start": v(-3.11, 196.47) * mm, "end": v(-4.1, 196.15) * mm});
            skLineSegment(sketch, "E289", {"start": v(-4.1, 196.15) * mm, "end": v(-5.1, 195.77) * mm});
            skLineSegment(sketch, "E290", {"start": v(-5.1, 195.77) * mm, "end": v(-6.03, 195.33) * mm});
            skLineSegment(sketch, "E291", {"start": v(-6.03, 195.33) * mm, "end": v(-6.94, 194.78) * mm});
            skLineSegment(sketch, "E292", {"start": v(-6.94, 194.78) * mm, "end": v(-7.79, 194.16) * mm});
            skLineSegment(sketch, "E293", {"start": v(-7.79, 194.16) * mm, "end": v(-8.6, 193.48) * mm});
            skLineSegment(sketch, "E294", {"start": v(-8.6, 193.48) * mm, "end": v(-9.33, 192.74) * mm});
            skLineSegment(sketch, "E295", {"start": v(-9.33, 192.74) * mm, "end": v(-10.01, 191.96) * mm});
            skLineSegment(sketch, "E296", {"start": v(-10.01, 191.96) * mm, "end": v(-10.63, 191.1) * mm});
            skLineSegment(sketch, "E297", {"start": v(-10.63, 191.1) * mm, "end": v(-11.15, 190.2) * mm});
            skLineSegment(sketch, "E298", {"start": v(-11.15, 190.2) * mm, "end": v(-11.62, 189.25) * mm});
            skLineSegment(sketch, "E299", {"start": v(-11.62, 189.25) * mm, "end": v(-12, 188.28) * mm});
            skLineSegment(sketch, "E300", {"start": v(-12, 188.28) * mm, "end": v(-12.3, 187.26) * mm});
            skLineSegment(sketch, "E301", {"start": v(-12.3, 187.26) * mm, "end": v(-12.5, 186.25) * mm});
            skLineSegment(sketch, "E302", {"start": v(-12.5, 186.25) * mm, "end": v(-12.64, 185.2) * mm});
            skLineSegment(sketch, "E303", {"start": v(-12.64, 185.2) * mm, "end": v(-12.7, 184.15) * mm});
            skLineSegment(sketch, "E304", {"start": v(-12.7, 184.15) * mm, "end": v(-12.64, 183.1) * mm});
            skLineSegment(sketch, "E305", {"start": v(-12.64, 183.1) * mm, "end": v(-12.5, 182.05) * mm});
            skLineSegment(sketch, "E306", {"start": v(-12.5, 182.05) * mm, "end": v(-12.3, 181.04) * mm});
            skLineSegment(sketch, "E307", {"start": v(-12.3, 181.04) * mm, "end": v(-12, 180.02) * mm});
            skLineSegment(sketch, "E308", {"start": v(-12, 180.02) * mm, "end": v(-11.62, 179.05) * mm});
            skLineSegment(sketch, "E309", {"start": v(-11.62, 179.05) * mm, "end": v(-11.15, 178.1) * mm});
            skLineSegment(sketch, "E310", {"start": v(-11.15, 178.1) * mm, "end": v(-10.63, 177.2) * mm});
            skLineSegment(sketch, "E311", {"start": v(-10.63, 177.2) * mm, "end": v(-10.01, 176.34) * mm});
            skLineSegment(sketch, "E312", {"start": v(-10.01, 176.34) * mm, "end": v(-9.33, 175.56) * mm});
            skLineSegment(sketch, "E313", {"start": v(-9.33, 175.56) * mm, "end": v(-8.6, 174.82) * mm});
            skLineSegment(sketch, "E314", {"start": v(-8.6, 174.82) * mm, "end": v(-7.79, 174.14) * mm});
            skLineSegment(sketch, "E315", {"start": v(-7.79, 174.14) * mm, "end": v(-6.94, 173.52) * mm});
            skLineSegment(sketch, "E316", {"start": v(-6.94, 173.52) * mm, "end": v(-6.03, 172.97) * mm});
            skLineSegment(sketch, "E317", {"start": v(-6.03, 172.97) * mm, "end": v(-5.1, 172.53) * mm});
            skLineSegment(sketch, "E318", {"start": v(-5.1, 172.53) * mm, "end": v(-4.1, 172.15) * mm});
            skLineSegment(sketch, "E319", {"start": v(-4.1, 172.15) * mm, "end": v(-3.11, 171.83) * mm});
            skLineSegment(sketch, "E320", {"start": v(-3.11, 171.83) * mm, "end": v(-2.07, 171.62) * mm});
            skLineSegment(sketch, "E321", {"start": v(-2.07, 171.62) * mm, "end": v(-1.04, 171.5) * mm});
            skLineSegment(sketch, "E322", {"start": v(-1.04, 171.5) * mm, "end": v(0, 171.45) * mm});
            skLineSegment(sketch, "E323", {"start": v(-6.35, 7.94) * mm, "end": v(-5.38, 7.98) * mm});
            skLineSegment(sketch, "E324", {"start": v(-5.38, 7.98) * mm, "end": v(-4.4, 8.1) * mm});
            skLineSegment(sketch, "E325", {"start": v(-4.4, 8.1) * mm, "end": v(-3.47, 8.32) * mm});
            skLineSegment(sketch, "E326", {"start": v(-3.47, 8.32) * mm, "end": v(-2.54, 8.61) * mm});
            skLineSegment(sketch, "E327", {"start": v(-2.54, 8.61) * mm, "end": v(-1.65, 8.97) * mm});
            skLineSegment(sketch, "E328", {"start": v(-1.65, 8.97) * mm, "end": v(-0.78, 9.42) * mm});
            skLineSegment(sketch, "E329", {"start": v(-0.78, 9.42) * mm, "end": v(0.04, 9.95) * mm});
            skLineSegment(sketch, "E330", {"start": v(0.04, 9.95) * mm, "end": v(0.8, 10.54) * mm});
            skLineSegment(sketch, "E331", {"start": v(0.8, 10.54) * mm, "end": v(1.52, 11.2) * mm});
            skLineSegment(sketch, "E332", {"start": v(1.52, 11.2) * mm, "end": v(2.18, 11.92) * mm});
            skLineSegment(sketch, "E333", {"start": v(2.18, 11.92) * mm, "end": v(2.77, 12.68) * mm});
            skLineSegment(sketch, "E334", {"start": v(2.77, 12.68) * mm, "end": v(3.28, 13.5) * mm});
            skLineSegment(sketch, "E335", {"start": v(3.28, 13.5) * mm, "end": v(3.73, 14.35) * mm});
            skLineSegment(sketch, "E336", {"start": v(3.73, 14.35) * mm, "end": v(4.1, 15.24) * mm});
            skLineSegment(sketch, "E337", {"start": v(4.1, 15.24) * mm, "end": v(4.4, 16.17) * mm});
            skLineSegment(sketch, "E338", {"start": v(4.4, 16.17) * mm, "end": v(4.61, 17.12) * mm});
            skLineSegment(sketch, "E339", {"start": v(4.61, 17.12) * mm, "end": v(4.72, 18.08) * mm});
            skLineSegment(sketch, "E340", {"start": v(4.72, 18.08) * mm, "end": v(4.76, 19.05) * mm});
            skLineSegment(sketch, "E341", {"start": v(4.76, 19.05) * mm, "end": v(4.72, 20.02) * mm});
            skLineSegment(sketch, "E342", {"start": v(4.72, 20.02) * mm, "end": v(4.61, 20.98) * mm});
            skLineSegment(sketch, "E343", {"start": v(4.61, 20.98) * mm, "end": v(4.4, 21.93) * mm});
            skLineSegment(sketch, "E344", {"start": v(4.4, 21.93) * mm, "end": v(4.1, 22.86) * mm});
            skLineSegment(sketch, "E345", {"start": v(4.1, 22.86) * mm, "end": v(3.73, 23.75) * mm});
            skLineSegment(sketch, "E346", {"start": v(3.73, 23.75) * mm, "end": v(3.28, 24.62) * mm});
            skLineSegment(sketch, "E347", {"start": v(3.28, 24.62) * mm, "end": v(2.77, 25.42) * mm});
            skLineSegment(sketch, "E348", {"start": v(2.77, 25.42) * mm, "end": v(2.18, 26.18) * mm});
            skLineSegment(sketch, "E349", {"start": v(2.18, 26.18) * mm, "end": v(1.52, 26.9) * mm});
            skLineSegment(sketch, "E350", {"start": v(1.52, 26.9) * mm, "end": v(0.8, 27.56) * mm});
            skLineSegment(sketch, "E351", {"start": v(0.8, 27.56) * mm, "end": v(0.04, 28.15) * mm});
            skLineSegment(sketch, "E352", {"start": v(0.04, 28.15) * mm, "end": v(-0.78, 28.68) * mm});
            skLineSegment(sketch, "E353", {"start": v(-0.78, 28.68) * mm, "end": v(-1.65, 29.13) * mm});
            skLineSegment(sketch, "E354", {"start": v(-1.65, 29.13) * mm, "end": v(-2.54, 29.49) * mm});
            skLineSegment(sketch, "E355", {"start": v(-2.54, 29.49) * mm, "end": v(-3.47, 29.78) * mm});
            skLineSegment(sketch, "E356", {"start": v(-3.47, 29.78) * mm, "end": v(-4.4, 30) * mm});
            skLineSegment(sketch, "E357", {"start": v(-4.4, 30) * mm, "end": v(-5.38, 30.12) * mm});
            skLineSegment(sketch, "E358", {"start": v(-5.38, 30.12) * mm, "end": v(-6.35, 30.16) * mm});
            skLineSegment(sketch, "E359", {"start": v(-6.35, 30.16) * mm, "end": v(-7.3, 30.12) * mm});
            skLineSegment(sketch, "E360", {"start": v(-7.3, 30.12) * mm, "end": v(-8.28, 30) * mm});
            skLineSegment(sketch, "E361", {"start": v(-8.28, 30) * mm, "end": v(-9.2, 29.78) * mm});
            skLineSegment(sketch, "E362", {"start": v(-9.2, 29.78) * mm, "end": v(-10.14, 29.49) * mm});
            skLineSegment(sketch, "E363", {"start": v(-10.14, 29.49) * mm, "end": v(-11.03, 29.13) * mm});
            skLineSegment(sketch, "E364", {"start": v(-11.03, 29.13) * mm, "end": v(-11.9, 28.68) * mm});
            skLineSegment(sketch, "E365", {"start": v(-11.9, 28.68) * mm, "end": v(-12.72, 28.15) * mm});
            skLineSegment(sketch, "E366", {"start": v(-12.72, 28.15) * mm, "end": v(-13.48, 27.56) * mm});
            skLineSegment(sketch, "E367", {"start": v(-13.48, 27.56) * mm, "end": v(-14.2, 26.9) * mm});
            skLineSegment(sketch, "E368", {"start": v(-14.2, 26.9) * mm, "end": v(-14.86, 26.18) * mm});
            skLineSegment(sketch, "E369", {"start": v(-14.86, 26.18) * mm, "end": v(-15.45, 25.42) * mm});
            skLineSegment(sketch, "E370", {"start": v(-15.45, 25.42) * mm, "end": v(-15.96, 24.62) * mm});
            skLineSegment(sketch, "E371", {"start": v(-15.96, 24.62) * mm, "end": v(-16.4, 23.75) * mm});
            skLineSegment(sketch, "E372", {"start": v(-16.4, 23.75) * mm, "end": v(-16.79, 22.86) * mm});
            skLineSegment(sketch, "E373", {"start": v(-16.79, 22.86) * mm, "end": v(-17.08, 21.93) * mm});
            skLineSegment(sketch, "E374", {"start": v(-17.08, 21.93) * mm, "end": v(-17.3, 20.98) * mm});
            skLineSegment(sketch, "E375", {"start": v(-17.3, 20.98) * mm, "end": v(-17.42, 20.02) * mm});
            skLineSegment(sketch, "E376", {"start": v(-17.42, 20.02) * mm, "end": v(-17.46, 19.05) * mm});
            skLineSegment(sketch, "E377", {"start": v(-17.46, 19.05) * mm, "end": v(-17.42, 18.08) * mm});
            skLineSegment(sketch, "E378", {"start": v(-17.42, 18.08) * mm, "end": v(-17.3, 17.12) * mm});
            skLineSegment(sketch, "E379", {"start": v(-17.3, 17.12) * mm, "end": v(-17.08, 16.17) * mm});
            skLineSegment(sketch, "E380", {"start": v(-17.08, 16.17) * mm, "end": v(-16.79, 15.24) * mm});
            skLineSegment(sketch, "E381", {"start": v(-16.79, 15.24) * mm, "end": v(-16.4, 14.35) * mm});
            skLineSegment(sketch, "E382", {"start": v(-16.4, 14.35) * mm, "end": v(-15.96, 13.5) * mm});
            skLineSegment(sketch, "E383", {"start": v(-15.96, 13.5) * mm, "end": v(-15.45, 12.68) * mm});
            skLineSegment(sketch, "E384", {"start": v(-15.45, 12.68) * mm, "end": v(-14.86, 11.92) * mm});
            skLineSegment(sketch, "E385", {"start": v(-14.86, 11.92) * mm, "end": v(-14.2, 11.2) * mm});
            skLineSegment(sketch, "E386", {"start": v(-14.2, 11.2) * mm, "end": v(-13.48, 10.54) * mm});
            skLineSegment(sketch, "E387", {"start": v(-13.48, 10.54) * mm, "end": v(-12.72, 9.95) * mm});
            skLineSegment(sketch, "E388", {"start": v(-12.72, 9.95) * mm, "end": v(-11.9, 9.42) * mm});
            skLineSegment(sketch, "E389", {"start": v(-11.9, 9.42) * mm, "end": v(-11.03, 8.97) * mm});
            skLineSegment(sketch, "E390", {"start": v(-11.03, 8.97) * mm, "end": v(-10.14, 8.61) * mm});
            skLineSegment(sketch, "E391", {"start": v(-10.14, 8.61) * mm, "end": v(-9.2, 8.32) * mm});
            skLineSegment(sketch, "E392", {"start": v(-9.2, 8.32) * mm, "end": v(-8.28, 8.1) * mm});
            skLineSegment(sketch, "E393", {"start": v(-8.28, 8.1) * mm, "end": v(-7.3, 7.98) * mm});
            skLineSegment(sketch, "E394", {"start": v(-7.3, 7.98) * mm, "end": v(-6.35, 7.94) * mm});
            skLineSegment(sketch, "E395", {"start": v(-25.4, 98.42) * mm, "end": v(-24.6, 99.4) * mm});
            skLineSegment(sketch, "E396", {"start": v(-24.6, 99.4) * mm, "end": v(-23.85, 100.44) * mm});
            skLineSegment(sketch, "E397", {"start": v(-23.85, 100.44) * mm, "end": v(-23.2, 101.5) * mm});
            skLineSegment(sketch, "E398", {"start": v(-23.2, 101.5) * mm, "end": v(-22.6, 102.62) * mm});
            skLineSegment(sketch, "E399", {"start": v(-22.6, 102.62) * mm, "end": v(-22.1, 103.76) * mm});
            skLineSegment(sketch, "E400", {"start": v(-22.1, 103.76) * mm, "end": v(-21.65, 104.94) * mm});
            skLineSegment(sketch, "E401", {"start": v(-21.65, 104.94) * mm, "end": v(-21.27, 106.15) * mm});
            skLineSegment(sketch, "E402", {"start": v(-21.27, 106.15) * mm, "end": v(-21, 107.38) * mm});
            skLineSegment(sketch, "E403", {"start": v(-21, 107.38) * mm, "end": v(-20.79, 108.6) * mm});
            skLineSegment(sketch, "E404", {"start": v(-20.79, 108.6) * mm, "end": v(-20.66, 109.88) * mm});
            skLineSegment(sketch, "E405", {"start": v(-20.66, 109.88) * mm, "end": v(-20.64, 111.12) * mm});
            skLineSegment(sketch, "E406", {"start": v(-20.64, 111.12) * mm, "end": v(-20.66, 112.37) * mm});
            skLineSegment(sketch, "E407", {"start": v(-20.66, 112.37) * mm, "end": v(-20.79, 113.64) * mm});
            skLineSegment(sketch, "E408", {"start": v(-20.79, 113.64) * mm, "end": v(-21, 114.87) * mm});
            skLineSegment(sketch, "E409", {"start": v(-21, 114.87) * mm, "end": v(-21.27, 116.1) * mm});
            skLineSegment(sketch, "E410", {"start": v(-21.27, 116.1) * mm, "end": v(-21.65, 117.3) * mm});
            skLineSegment(sketch, "E411", {"start": v(-21.65, 117.3) * mm, "end": v(-22.1, 118.5) * mm});
            skLineSegment(sketch, "E412", {"start": v(-22.1, 118.5) * mm, "end": v(-22.6, 119.63) * mm});
            skLineSegment(sketch, "E413", {"start": v(-22.6, 119.63) * mm, "end": v(-23.2, 120.76) * mm});
            skLineSegment(sketch, "E414", {"start": v(-23.2, 120.76) * mm, "end": v(-23.85, 121.81) * mm});
            skLineSegment(sketch, "E415", {"start": v(-23.85, 121.81) * mm, "end": v(-24.6, 122.85) * mm});
            skLineSegment(sketch, "E416", {"start": v(-24.6, 122.85) * mm, "end": v(-25.4, 123.82) * mm});
            skSolve(sketch);
        }
        {
            var Q0;
            Q0 = qSketchRegion(id + "F0", true);
            extrude(context, id + "F1", {"entities" : qUnion([Q0]), "depth" : 9.52 * mm, "offsetDistance" : 25.4 * mm});
        }
    });
